# Revit family: French-PGT-Aluminum_Preferred-FD750-Xd
name_source: partatom
category: Doors
revit_build: Autodesk Revit 2015 (Build: 20160512_1515(x64)
units: mm (PartAtom-declared; Revit-internal decimal feet)

## types (1)
- Refer to Type Catalog
    Analytic Construction = <None>
    Assembly Code = B2030110
    BP Calc = 4 7/16"
    CL Offset From Exterior = 2"
    Color Glass = Glass - PGT - Clear
    Custom Design Note = The types included show default grid/size configurations.  Please reference the 'Product Style Guide' to see all standard configurations and restrictions before creating custom designs.  Please contact PGT Industries with any questions regarding custom designs.
    Description = Aluminum Preferred Frech Door
    Finish = Metal - PGT - Paint - White
    Function = Exterior
    Grid = Yes
    Grid Layout Note = To edit the grid layout ensure the 'Grid' parameter is turned on and then select an option from the 'Grid Type' drop down.  Please refer to the 'Product Style Guide' for standard configurations and restrictions.
    Grid Type = Face_Based_Mullion_ Glass : 2C4R
    Hardware Height = 36"
    Hardware Material = Steel AISI 4620
    Height = 90"
    Manufacturer = PGT Industries
    Maximum Size = 37” x 95 3/4”
    Minimum Size = 20” x 35 3/4”
    Model = FD750 X
    Product Page URL = http://www.pgtindustries.com
    Product Style Guide = http://www.pgtindustries.com
    Rough Height = 91 9/32"
    Rough Width = 38 9/16"
    Type Comments = Single Door
    URL = http://www.pgtindustries.com
    Wall Closure = By host
    Width = 36"

## geometry (parser evidence)
native form markers: Sweep x29
no freeform markers — native parametric forms only
